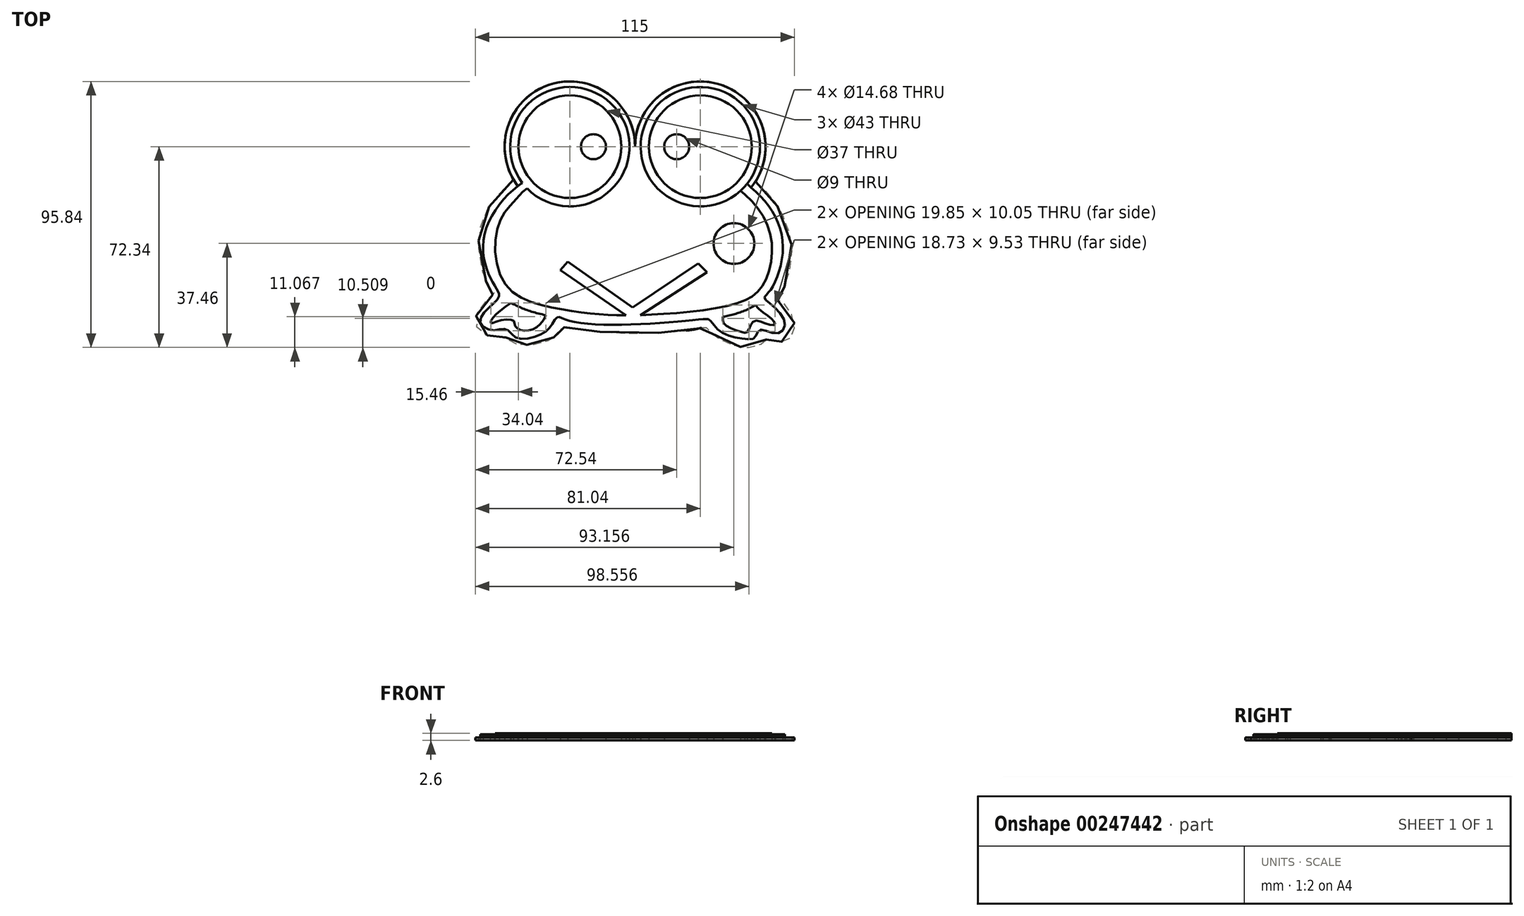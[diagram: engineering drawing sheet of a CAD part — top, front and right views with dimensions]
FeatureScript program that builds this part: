
annotation { "Feature Type Name" : "Feature", "Feature Type Description" : "" }
export const myFeature = defineFeature(function(context is Context, id is Id, definition is map)
    precondition{}
    {
        {
            var Q0;
            Q0=qCreatedBy(makeId("Top.planeOp"),FACE);
            var sketch = newSketch(context, id + "F0", { "sketchPlane" : qUnion([Q0])});
            skArc(sketch, "E0", {"start": v(0, 0) * mm, "mid": v(-32.27, 21.8) * mm, "end": v(-40.45, -16.28) * mm});
            skLineSegment(sketch, "E1", {"start": v(0, 0) * mm, "end": v(0, 32.9) * mm, "construction": true});
            skArc(sketch, "E2.MirrorC", {"start": v(0, 0) * mm, "mid": v(32.88, 21.54) * mm, "end": v(39.5, -17.2) * mm});
            skCircle(sketch, "E3", {"center": v(-15, 0) * mm, "radius": 4.5 * mm});
            skCircle(sketch, "E4.MirrorC", {"center": v(15, 0) * mm, "radius": 4.5 * mm});
            skCircle(sketch, "E5", {"center": v(-23.5, 0) * mm, "radius": 21.5 * mm});
            skCircle(sketch, "E6.MirrorC", {"center": v(23.5, 0) * mm, "radius": 21.5 * mm});
            skCircle(sketch, "E7", {"center": v(-23.5, 0) * mm, "radius": 18.5 * mm});
            skCircle(sketch, "E8.MirrorC", {"center": v(23.5, 0) * mm, "radius": 18.5 * mm});
            skFitSpline(sketch, "E9", {"points": [v(-40.58, -13.06) * mm, v(-54.39, -32.33) * mm, v(-51.31, -48.91) * mm, v(-48.96, -53.83) * mm, v(-52.4, -57.72) * mm, v(-55.74, -63.13) * mm, v(-51.26, -66.14) * mm, v(-46.44, -65.76) * mm, v(-42.61, -68.88) * mm, v(-34.3, -67.78) * mm, v(-30.2, -64.45) * mm, v(-28.01, -61.44) * mm, v(-24.73, -62.42) * mm, v(-1.13, -64.06) * mm, v(24.92, -62.13) * mm, v(27.01, -62.5) * mm, v(30.32, -66.31) * mm, v(38.07, -69.05) * mm, v(43.18, -68.74) * mm, v(44.93, -66) * mm, v(50.97, -67.3) * mm, v(54, -63.47) * mm, v(48.5, -56.44) * mm, v(46.63, -54.44) * mm, v(48.93, -51.42) * mm, v(53.1, -33.55) * mm, v(41.84, -14.7) * mm], "startDerivative": vector(-272.03, -169.05) * mm, "endDerivative": vector(-267.1, 228.3) * mm});
            skLineSegment(sketch, "E10", {"start": v(-26.94, -44.44) * mm, "end": v(-24.31, -41.45) * mm});
            skLineSegment(sketch, "E11", {"start": v(-24.31, -41.45) * mm, "end": v(-0.83, -57.91) * mm});
            skLineSegment(sketch, "E12", {"start": v(-0.83, -57.91) * mm, "end": v(22.76, -42.01) * mm});
            skLineSegment(sketch, "E13", {"start": v(22.76, -42.01) * mm, "end": v(25.91, -45.21) * mm});
            skLineSegment(sketch, "E14", {"start": v(25.91, -45.21) * mm, "end": v(1.45, -61) * mm});
            skLineSegment(sketch, "E15", {"start": v(1.45, -61) * mm, "end": v(-3, -61) * mm});
            skLineSegment(sketch, "E16", {"start": v(-3, -61) * mm, "end": v(-26.94, -44.44) * mm});
            skCircle(sketch, "E17", {"center": v(-35.62, -34.88) * mm, "radius": 7.34 * mm});
            skCircle(sketch, "E18.MirrorC", {"center": v(35.62, -34.88) * mm, "radius": 7.34 * mm});
            skFitSpline(sketch, "E19", {"points": [v(-40.45, -16.28) * mm, v(-49.2, -28.03) * mm, v(-46.66, -49.7) * mm, v(-29.22, -58.07) * mm, v(-12.9, -60.41) * mm, v(3.7, -60.62) * mm, v(35.71, -56.76) * mm, v(46.28, -49.46) * mm, v(49, -32.95) * mm, v(39.5, -17.2) * mm], "startDerivative": vector(-106.9, -127.15) * mm, "endDerivative": vector(-138.07, 119.36) * mm});
            skFitSpline(sketch, "E20", {"points": [v(-48.96, -53.83) * mm, v(-28.01, -61.44) * mm], "startDerivative": vector(19.15, -11.25) * mm, "endDerivative": vector(32.1, -4.95) * mm});
            skFitSpline(sketch, "E21", {"points": [v(-44.73, -56.25) * mm, v(-51.4, -61.88) * mm, v(-51.91, -63.52) * mm, v(-48.79, -62.68) * mm, v(-43.75, -62.74) * mm, v(-43.23, -64.5) * mm, v(-40.8, -66.13) * mm, v(-36.35, -65.59) * mm, v(-32.16, -60.7) * mm], "startDerivative": vector(-46.22, -34.5) * mm, "endDerivative": vector(16.79, 43.44) * mm});
            skFitSpline(sketch, "E22", {"points": [v(26.44, -62.17) * mm, v(46.63, -54.44) * mm], "startDerivative": vector(19.8, 3.32) * mm, "endDerivative": vector(18.04, 17.17) * mm});
            skFitSpline(sketch, "E23", {"points": [v(31.65, -61.28) * mm, v(32.18, -63.96) * mm, v(38.42, -66.78) * mm, v(40.52, -66.75) * mm, v(42.62, -62.92) * mm, v(47.62, -63.89) * mm, v(50.34, -64) * mm, v(49, -61.86) * mm, v(43.28, -57.06) * mm], "startDerivative": vector(-2.74, -27.83) * mm, "endDerivative": vector(-25.37, 35.67) * mm});
            skFitSpline(sketch, "E24", {"points": [v(-43.83, -11.78) * mm, v(-53.16, -22.6) * mm, v(-56.39, -36.38) * mm, v(-52.23, -51.09) * mm, v(-50.65, -52.46) * mm, v(-51.85, -53.71) * mm, v(-56.99, -60.28) * mm, v(-56.44, -65.8) * mm, v(-49.88, -68.64) * mm, v(-46.98, -68.37) * mm, v(-46, -69.74) * mm, v(-38.83, -71.38) * mm, v(-30.41, -69.4) * mm, v(-26.53, -66.13) * mm, v(-26.15, -65.14) * mm, v(-24.34, -65.3) * mm, v(0.87, -67.27) * mm, v(23.5, -65.36) * mm, v(25.36, -64.92) * mm, v(26.62, -66.24) * mm, v(33.51, -70.83) * mm, v(44.56, -71.6) * mm, v(48.06, -68.97) * mm, v(49.31, -69.63) * mm, v(54.3, -69.95) * mm, v(57.46, -64.81) * mm, v(52.92, -55.9) * mm, v(50.57, -55.08) * mm, v(51.83, -53.66) * mm, v(56.53, -38.78) * mm, v(51.28, -21.34) * mm, v(43.37, -12.54) * mm], "startDerivative": vector(-221.88, -218.4) * mm, "endDerivative": vector(-221.71, 192.9) * mm});
            skFitSpline(sketch, "E25", {"points": [v(41.84, -14.7) * mm, v(40.36, -13.34) * mm], "startDerivative": vector(-1.5, 1.36) * mm, "endDerivative": vector(-1.5, 1.36) * mm});
            skFitSpline(sketch, "E26", {"points": [v(-40.45, -16.28) * mm, v(-38.9, -15.01) * mm], "startDerivative": vector(1.56, 1.27) * mm, "endDerivative": vector(1.56, 1.27) * mm});
            skFitSpline(sketch, "E27", {"points": [v(39.5, -17.2) * mm, v(37.93, -15.94) * mm], "startDerivative": vector(-1.59, 1.29) * mm, "endDerivative": vector(-1.59, 1.29) * mm});
            skSolve(sketch);
        }
        {
            var Q0;
            Q0=makeQuery(id+"F0.imprint","IMPRINT",FACE,{"disambiguationData":[TD([[makeQuery(id+"F0.imprint","IMPRINT",EDGE,{"derivedFrom":sQuery(id+"F0.wireOp",EDGE,"E4.MirrorC")}),-1.0]])]});
            var Q1;
            Q1=makeQuery(id+"F0.imprint","IMPRINT",FACE,{"disambiguationData":[TD([[makeQuery(id+"F0.imprint","IMPRINT",EDGE,{"derivedFrom":sQuery(id+"F0.wireOp",EDGE,"E3")}),1.0]])]});
            var Q2;
            Q2=makeQuery(id+"F0.imprint","IMPRINT",FACE,{"disambiguationData":[TD([[makeQuery(id+"F0.imprint","IMPRINT",EDGE,{"derivedFrom":sQuery(id+"F0.wireOp",EDGE,"E17")}),1.0]])]});
            var Q3;
            Q3=makeQuery(id+"F0.imprint","IMPRINT",FACE,{"disambiguationData":[TD([[makeQuery(id+"F0.imprint","IMPRINT",EDGE,{"derivedFrom":sQuery(id+"F0.wireOp",EDGE,"E18.MirrorC")}),-1.0]])]});
            var Q4;
            Q4=makeQuery(id+"F0.imprint","IMPRINT",FACE,{"disambiguationData":[TD([[makeQuery(id+"F0.imprint","IMPRINT",EDGE,{"derivedFrom":sQuery(id+"F0.wireOp",EDGE,"E3")}),-1.0]])]});
            var Q5;
            Q5=makeQuery(id+"F0.imprint","IMPRINT",FACE,{"disambiguationData":[TD([[makeQuery(id+"F0.imprint","IMPRINT",EDGE,{"derivedFrom":sQuery(id+"F0.wireOp",EDGE,"E5")}),-1.0]])]});
            var Q6;
            {var subQ4=sQuery(id+"F0.wireOp",EDGE,"E23");Q6=makeQuery(id+"F0.imprint","IMPRINT",FACE,{"disambiguationData":[TD([[makeQuery(id+"F0.imprint","IMPRINT",EDGE,{"derivedFrom":subQ4}),-1.0]])]});}
            var Q7;
            {var subQ16=sQuery(id+"F0.wireOp",EDGE,"E15");Q7=makeQuery(id+"F0.imprint","IMPRINT",FACE,{"disambiguationData":[TD([[makeQuery(id+"F0.imprint","IMPRINT",EDGE,{"derivedFrom":subQ16}),1.0]])]});}
            var Q8;
            {var subQ10=sQuery(id+"F0.wireOp",EDGE,"E24");Q8=makeQuery(id+"F0.imprint","IMPRINT",FACE,{"disambiguationData":[TD([[makeQuery(id+"F0.imprint","IMPRINT",EDGE,{"derivedFrom":subQ10}),1.0]])]});}
            var Q9;
            {var subQ0=sQuery(id+"F0.wireOp",EDGE,"E23");Q9=makeQuery(id+"F0.imprint","IMPRINT",FACE,{"disambiguationData":[TD([[makeQuery(id+"F0.imprint","IMPRINT",EDGE,{"derivedFrom":subQ0}),1.0]])]});}
            var Q10;
            Q10=makeQuery(id+"F0.imprint","IMPRINT",FACE,{"disambiguationData":[TD([[makeQuery(id+"F0.imprint","IMPRINT",EDGE,{"derivedFrom":sQuery(id+"F0.wireOp",EDGE,"E4.MirrorC")}),1.0]])]});
            var Q11;
            Q11=makeQuery(id+"F0.imprint","IMPRINT",FACE,{"disambiguationData":[TD([[makeQuery(id+"F0.imprint","IMPRINT",EDGE,{"derivedFrom":sQuery(id+"F0.wireOp",EDGE,"E5")}),1.0]])]});
            var Q12;
            {var subQ2=sQuery(id+"F0.wireOp",EDGE,"E10");Q12=makeQuery(id+"F0.imprint","IMPRINT",FACE,{"disambiguationData":[TD([[makeQuery(id+"F0.imprint","IMPRINT",EDGE,{"derivedFrom":subQ2}),-1.0]])]});}
            var Q13;
            Q13=makeQuery(id+"F0.imprint","IMPRINT",FACE,{"disambiguationData":[TD([[makeQuery(id+"F0.imprint","IMPRINT",EDGE,{"derivedFrom":sQuery(id+"F0.wireOp",EDGE,"E6.MirrorC")}),-1.0]])]});
            var Q14;
            {var subQ0=sQuery(id+"F0.wireOp",EDGE,"E21");Q14=makeQuery(id+"F0.imprint","IMPRINT",FACE,{"disambiguationData":[TD([[makeQuery(id+"F0.imprint","IMPRINT",EDGE,{"derivedFrom":subQ0}),1.0]])]});}
            var Q15;
            {var subQ4=sQuery(id+"F0.wireOp",EDGE,"E21");Q15=makeQuery(id+"F0.imprint","IMPRINT",FACE,{"disambiguationData":[TD([[makeQuery(id+"F0.imprint","IMPRINT",EDGE,{"derivedFrom":subQ4}),-1.0]])]});}
            var Q16;
            {var subQ0=sQuery(id+"F0.wireOp",EDGE,"E15");Q16=makeQuery(id+"F0.imprint","IMPRINT",FACE,{"disambiguationData":[TD([[makeQuery(id+"F0.imprint","IMPRINT",EDGE,{"derivedFrom":subQ0}),-1.0]])]});}
            var Q17;
            {var subQ9=sQuery(id+"F0.wireOp",EDGE,"E10");Q17=makeQuery(id+"F0.imprint","IMPRINT",FACE,{"disambiguationData":[TD([[makeQuery(id+"F0.imprint","IMPRINT",EDGE,{"derivedFrom":subQ9}),1.0]])]});}
            var Q18;
            {var subQ2=sQuery(id+"F0.wireOp",EDGE,"E25");Q18=makeQuery(id+"F0.imprint","IMPRINT",FACE,{"disambiguationData":[TD([[makeQuery(id+"F0.imprint","IMPRINT",EDGE,{"derivedFrom":subQ2}),1.0]])]});}
            extrude(context, id + "F1", {"entities" : qUnion([Q0, Q1, Q2, Q3, Q4, Q5, Q6, Q7, Q8, Q9, Q10, Q11, Q12, Q13, Q14, Q15, Q16, Q17, Q18]), "depth" : 1 * mm});
        }
        {
            var Q0;
            Q0=makeQuery(id+"F0.imprint","IMPRINT",FACE,{"disambiguationData":[TD([[makeQuery(id+"F0.imprint","IMPRINT",EDGE,{"derivedFrom":sQuery(id+"F0.wireOp",EDGE,"E7")}),-1.0]])]});
            var Q1;
            Q1=makeQuery(id+"F0.imprint","IMPRINT",FACE,{"disambiguationData":[TD([[makeQuery(id+"F0.imprint","IMPRINT",EDGE,{"derivedFrom":sQuery(id+"F0.wireOp",EDGE,"E3")}),-1.0]])]});
            var Q2;
            Q2=makeQuery(id+"F0.imprint","IMPRINT",FACE,{"disambiguationData":[TD([[makeQuery(id+"F0.imprint","IMPRINT",EDGE,{"derivedFrom":sQuery(id+"F0.wireOp",EDGE,"E3")}),1.0]])]});
            var Q3;
            Q3=makeQuery(id+"F0.imprint","IMPRINT",FACE,{"disambiguationData":[TD([[makeQuery(id+"F0.imprint","IMPRINT",EDGE,{"derivedFrom":sQuery(id+"F0.wireOp",EDGE,"E8.MirrorC")}),1.0]])]});
            var Q4;
            Q4=makeQuery(id+"F0.imprint","IMPRINT",FACE,{"disambiguationData":[TD([[makeQuery(id+"F0.imprint","IMPRINT",EDGE,{"derivedFrom":sQuery(id+"F0.wireOp",EDGE,"E4.MirrorC")}),-1.0]])]});
            var Q5;
            Q5=makeQuery(id+"F0.imprint","IMPRINT",FACE,{"disambiguationData":[TD([[makeQuery(id+"F0.imprint","IMPRINT",EDGE,{"derivedFrom":sQuery(id+"F0.wireOp",EDGE,"E4.MirrorC")}),1.0]])]});
            var Q6;
            {var subQ2=sQuery(id+"F0.wireOp",EDGE,"E10");Q6=makeQuery(id+"F0.imprint","IMPRINT",FACE,{"disambiguationData":[TD([[makeQuery(id+"F0.imprint","IMPRINT",EDGE,{"derivedFrom":subQ2}),-1.0]])]});}
            var Q7;
            Q7=makeQuery(id+"F0.imprint","IMPRINT",FACE,{"disambiguationData":[TD([[makeQuery(id+"F0.imprint","IMPRINT",EDGE,{"derivedFrom":sQuery(id+"F0.wireOp",EDGE,"E17")}),1.0]])]});
            var Q8;
            Q8=makeQuery(id+"F0.imprint","IMPRINT",FACE,{"disambiguationData":[TD([[makeQuery(id+"F0.imprint","IMPRINT",EDGE,{"derivedFrom":sQuery(id+"F0.wireOp",EDGE,"E18.MirrorC")}),-1.0]])]});
            var Q9;
            {var subQ1=sQuery(id+"F0.wireOp",EDGE,"E15");Q9=makeQuery(id+"F0.imprint","IMPRINT",FACE,{"disambiguationData":[TD([[makeQuery(id+"F0.imprint","IMPRINT",EDGE,{"derivedFrom":subQ1}),1.0]])]});}
            var Q10;
            {var subQ4=sQuery(id+"F0.wireOp",EDGE,"E23");Q10=makeQuery(id+"F0.imprint","IMPRINT",FACE,{"disambiguationData":[TD([[makeQuery(id+"F0.imprint","IMPRINT",EDGE,{"derivedFrom":subQ4}),-1.0]])]});}
            var Q11;
            {var subQ4=sQuery(id+"F0.wireOp",EDGE,"E21");Q11=makeQuery(id+"F0.imprint","IMPRINT",FACE,{"disambiguationData":[TD([[makeQuery(id+"F0.imprint","IMPRINT",EDGE,{"derivedFrom":subQ4}),-1.0]])]});}
            var Q12;
            {var subQ0=sQuery(id+"F0.wireOp",EDGE,"E26");Q12=makeQuery(id+"F0.imprint","IMPRINT",FACE,{"disambiguationData":[TD([[makeQuery(id+"F0.imprint","IMPRINT",EDGE,{"derivedFrom":subQ0}),1.0]])]});}
            var Q13;
            {var subQ2=sQuery(id+"F0.wireOp",EDGE,"E25");Q13=makeQuery(id+"F0.imprint","IMPRINT",FACE,{"disambiguationData":[TD([[makeQuery(id+"F0.imprint","IMPRINT",EDGE,{"derivedFrom":subQ2}),1.0]])]});}
            var Q14;
            {var subQ0=sQuery(id+"F0.wireOp",EDGE,"E15");Q14=makeQuery(id+"F0.imprint","IMPRINT",FACE,{"disambiguationData":[TD([[makeQuery(id+"F0.imprint","IMPRINT",EDGE,{"derivedFrom":subQ0}),-1.0]])]});}
            extrude(context, id + "F2", {"entities" : qUnion([Q0, Q1, Q2, Q3, Q4, Q5, Q6, Q7, Q8, Q9, Q10, Q11, Q12, Q13, Q14]), "depth" : (1 + 0.4 + 0.4) * mm});
        }
        {
            var Q0;
            Q0=makeQuery(id+"F0.imprint","IMPRINT",FACE,{"disambiguationData":[TD([[makeQuery(id+"F0.imprint","IMPRINT",EDGE,{"derivedFrom":sQuery(id+"F0.wireOp",EDGE,"E3")}),1.0]])]});
            var Q1;
            Q1=makeQuery(id+"F0.imprint","IMPRINT",FACE,{"disambiguationData":[TD([[makeQuery(id+"F0.imprint","IMPRINT",EDGE,{"derivedFrom":sQuery(id+"F0.wireOp",EDGE,"E7")}),-1.0]])]});
            var Q2;
            {var subQ0=sQuery(id+"F0.wireOp",EDGE,"E26");Q2=makeQuery(id+"F0.imprint","IMPRINT",FACE,{"disambiguationData":[TD([[makeQuery(id+"F0.imprint","IMPRINT",EDGE,{"derivedFrom":subQ0}),1.0]])]});}
            var Q3;
            {var subQ1=sQuery(id+"F0.wireOp",EDGE,"E15");Q3=makeQuery(id+"F0.imprint","IMPRINT",FACE,{"disambiguationData":[TD([[makeQuery(id+"F0.imprint","IMPRINT",EDGE,{"derivedFrom":subQ1}),1.0]])]});}
            var Q4;
            Q4=makeQuery(id+"F0.imprint","IMPRINT",FACE,{"disambiguationData":[TD([[makeQuery(id+"F0.imprint","IMPRINT",EDGE,{"derivedFrom":sQuery(id+"F0.wireOp",EDGE,"E17")}),1.0]])]});
            var Q5;
            Q5=makeQuery(id+"F0.imprint","IMPRINT",FACE,{"disambiguationData":[TD([[makeQuery(id+"F0.imprint","IMPRINT",EDGE,{"derivedFrom":sQuery(id+"F0.wireOp",EDGE,"E18.MirrorC")}),-1.0]])]});
            var Q6;
            {var subQ2=sQuery(id+"F0.wireOp",EDGE,"E10");Q6=makeQuery(id+"F0.imprint","IMPRINT",FACE,{"disambiguationData":[TD([[makeQuery(id+"F0.imprint","IMPRINT",EDGE,{"derivedFrom":subQ2}),-1.0]])]});}
            var Q7;
            {var subQ4=sQuery(id+"F0.wireOp",EDGE,"E21");Q7=makeQuery(id+"F0.imprint","IMPRINT",FACE,{"disambiguationData":[TD([[makeQuery(id+"F0.imprint","IMPRINT",EDGE,{"derivedFrom":subQ4}),-1.0]])]});}
            var Q8;
            {var subQ4=sQuery(id+"F0.wireOp",EDGE,"E23");Q8=makeQuery(id+"F0.imprint","IMPRINT",FACE,{"disambiguationData":[TD([[makeQuery(id+"F0.imprint","IMPRINT",EDGE,{"derivedFrom":subQ4}),-1.0]])]});}
            var Q9;
            {var subQ2=sQuery(id+"F0.wireOp",EDGE,"E25");Q9=makeQuery(id+"F0.imprint","IMPRINT",FACE,{"disambiguationData":[TD([[makeQuery(id+"F0.imprint","IMPRINT",EDGE,{"derivedFrom":subQ2}),1.0]])]});}
            var Q10;
            Q10=makeQuery(id+"F0.imprint","IMPRINT",FACE,{"disambiguationData":[TD([[makeQuery(id+"F0.imprint","IMPRINT",EDGE,{"derivedFrom":sQuery(id+"F0.wireOp",EDGE,"E8.MirrorC")}),1.0]])]});
            var Q11;
            Q11=makeQuery(id+"F0.imprint","IMPRINT",FACE,{"disambiguationData":[TD([[makeQuery(id+"F0.imprint","IMPRINT",EDGE,{"derivedFrom":sQuery(id+"F0.wireOp",EDGE,"E4.MirrorC")}),-1.0]])]});
            var Q12;
            {var subQ0=sQuery(id+"F0.wireOp",EDGE,"E15");Q12=makeQuery(id+"F0.imprint","IMPRINT",FACE,{"disambiguationData":[TD([[makeQuery(id+"F0.imprint","IMPRINT",EDGE,{"derivedFrom":subQ0}),-1.0]])]});}
            extrude(context, id + "F3", {"entities" : qUnion([Q0, Q1, Q2, Q3, Q4, Q5, Q6, Q7, Q8, Q9, Q10, Q11, Q12]), "depth" : (1 + 0.4 + 0.4 + 0.4) * mm});
        }
        {
            var Q0;
            Q0=makeQuery(id+"F0.imprint","IMPRINT",FACE,{"disambiguationData":[TD([[makeQuery(id+"F0.imprint","IMPRINT",EDGE,{"derivedFrom":sQuery(id+"F0.wireOp",EDGE,"E17")}),1.0]])]});
            var Q1;
            Q1=makeQuery(id+"F0.imprint","IMPRINT",FACE,{"disambiguationData":[TD([[makeQuery(id+"F0.imprint","IMPRINT",EDGE,{"derivedFrom":sQuery(id+"F0.wireOp",EDGE,"E18.MirrorC")}),-1.0]])]});
            extrude(context, id + "F4", {"entities" : qUnion([Q0, Q1]), "depth" : (1 + 0.4 + 0.4 + 0.4 + 0.4) * mm});
        }
    });
